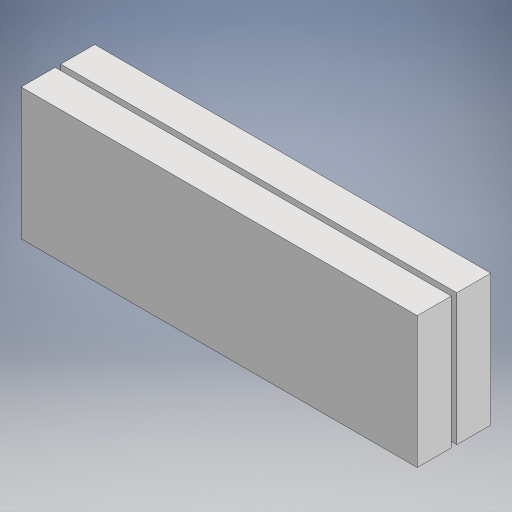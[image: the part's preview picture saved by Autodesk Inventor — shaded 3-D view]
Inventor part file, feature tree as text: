
AUTODESK INVENTOR PART (.ipt)
format: ipt  version: 2023.2 (Build 272271000, 271)  size: 201,216 bytes
history: native  units: in
note: dims shown in document units (in); Inventor stores cm internally (conversion verified against a paired STEP export)
features: extrude x1, sketch x1
ambient origin geometry x8: Origin, YZ Plane, XZ Plane, XY Plane, X Axis, Y Axis, Z Axis, Center Point
bodies: Solid1 (feature_tree)
feature tree (2):
  extrude  "Extrusion1"  Depth=6.5in
  sketch  "Sketch2"  dims[d3=11.625in d4=6.5in d5=0.5in d6=35.0in d7=0.0in]
